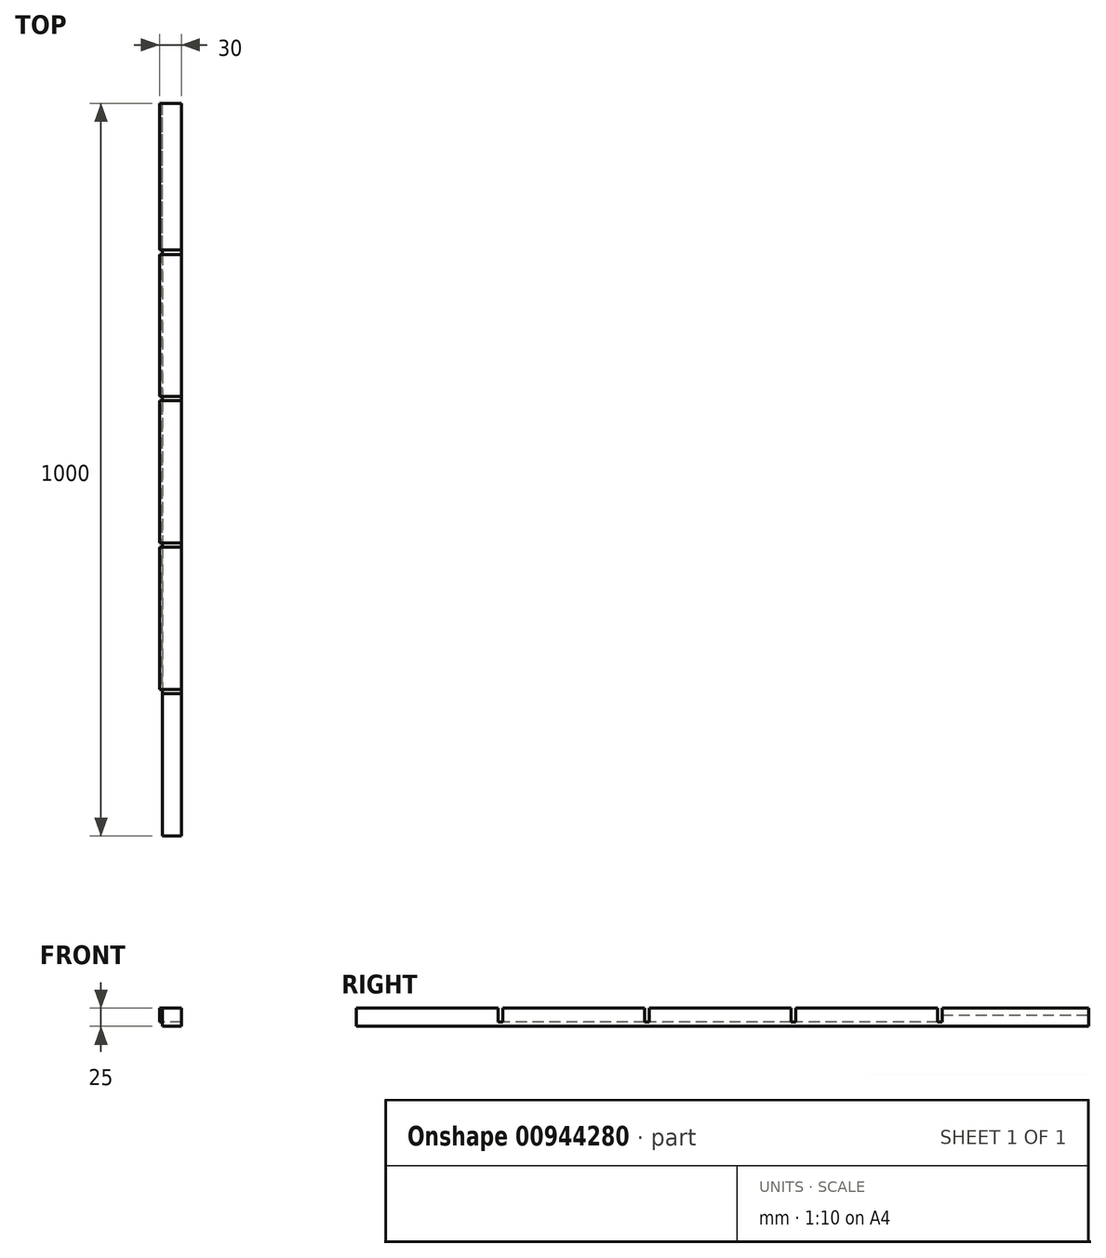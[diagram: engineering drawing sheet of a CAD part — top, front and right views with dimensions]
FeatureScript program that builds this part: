
annotation { "Feature Type Name" : "Feature", "Feature Type Description" : "" }
export const myFeature = defineFeature(function(context is Context, id is Id, definition is map)
    precondition{}
    {
        {
            var Q0;
            Q0=qCreatedBy(makeId("Top.planeOp"),FACE);
            var sketch = newSketch(context, id + "F0", { "sketchPlane" : qUnion([Q0])});
            skLineSegment(sketch, "E0.bottom", {"start": v(0, 0) * mm, "end": v(-30, 0) * mm});
            skLineSegment(sketch, "E0.top", {"start": v(0, 1000) * mm, "end": v(-30, 1000) * mm});
            skLineSegment(sketch, "E0.left", {"start": v(0, 0) * mm, "end": v(0, 1000) * mm});
            skLineSegment(sketch, "E0.right", {"start": v(-30, 0) * mm, "end": v(-30, 1000) * mm});
            skSolve(sketch);
        }
        {
            var Q0;
            Q0 = qSketchRegion(id + "F0", true);
            extrude(context, id + "F1", {"entities" : qUnion([Q0]), "depth" : 25 * mm, "offsetDistance" : 25 * mm});
        }
        {
            var Q0;
            Q0=makeQuery(id+"F1.opExtrude","SWEPT_FACE",FACE,{"disambiguationData":[OSD([sQuery(id+"F0.wireOp",EDGE,"E0.right")])]});
            var sketch = newSketch(context, id + "F2", { "sketchPlane" : qUnion([Q0])});
            skLineSegment(sketch, "E1", {"start": v(-800, 25) * mm, "end": v(-800, 0) * mm, "construction": true});
            skLineSegment(sketch, "E2.bottom", {"start": v(-800, 25) * mm, "end": v(-794, 25) * mm});
            skLineSegment(sketch, "E2.top", {"start": v(-800, 6) * mm, "end": v(-794, 6) * mm});
            skLineSegment(sketch, "E2.left", {"start": v(-800, 25) * mm, "end": v(-800, 6) * mm});
            skLineSegment(sketch, "E2.right", {"start": v(-794, 25) * mm, "end": v(-794, 6) * mm});
            skLineSegment(sketch, "E3.1.0.0", {"start": v(-600, 25) * mm, "end": v(-600, 6) * mm});
            skLineSegment(sketch, "E3.1.0.1", {"start": v(-600, 25) * mm, "end": v(-594, 25) * mm});
            skLineSegment(sketch, "E3.1.0.2", {"start": v(-594, 25) * mm, "end": v(-594, 6) * mm});
            skLineSegment(sketch, "E3.1.0.3", {"start": v(-600, 6) * mm, "end": v(-594, 6) * mm});
            skLineSegment(sketch, "E3.2.0.0", {"start": v(-400, 25) * mm, "end": v(-400, 6) * mm});
            skLineSegment(sketch, "E3.2.0.1", {"start": v(-400, 25) * mm, "end": v(-394, 25) * mm});
            skLineSegment(sketch, "E3.2.0.2", {"start": v(-394, 25) * mm, "end": v(-394, 6) * mm});
            skLineSegment(sketch, "E3.2.0.3", {"start": v(-400, 6) * mm, "end": v(-394, 6) * mm});
            skLineSegment(sketch, "E3.3.0.0", {"start": v(-200, 25) * mm, "end": v(-200, 6) * mm});
            skLineSegment(sketch, "E3.3.0.1", {"start": v(-200, 25) * mm, "end": v(-194, 25) * mm});
            skLineSegment(sketch, "E3.3.0.2", {"start": v(-194, 25) * mm, "end": v(-194, 6) * mm});
            skLineSegment(sketch, "E3.3.0.3", {"start": v(-200, 6) * mm, "end": v(-194, 6) * mm});
            skLineSegment(sketch, "E3.direction1", {"start": v(-800, 6) * mm, "end": v(-600, 6) * mm, "construction": true});
            skSolve(sketch);
        }
        {
            var Q0;
            Q0=makeQuery(id+"F2.imprint","IMPRINT",FACE,{"disambiguationData":[TD([[makeQuery(id+"F2.imprint","IMPRINT",EDGE,{"derivedFrom":sQuery(id+"F2.wireOp",EDGE,"E2.bottom")}),1.0]])]});
            extrude(context, id + "F3", {"entities" : qUnion([Q0]), "operationType" : NewBodyOperationType.REMOVE, "endBound" : BoundingType.THROUGH_ALL, "oppositeDirection" : true, "depth" : 25 * mm, "offsetDistance" : 25 * mm});
        }
        {
            var Q0;
            Q0 = qSketchRegion(id + "F2", true);
            extrude(context, id + "F4", {"entities" : qUnion([Q0]), "operationType" : NewBodyOperationType.REMOVE, "endBound" : BoundingType.THROUGH_ALL, "oppositeDirection" : true, "depth" : 25 * mm, "offsetDistance" : 25 * mm});
        }
        {
            var Q0;
            Q0=makeQuery(id+"F1.opExtrude","SWEPT_FACE",FACE,{"disambiguationData":[OSD([sQuery(id+"F0.wireOp",EDGE,"E0.right")])]});
            var sketch = newSketch(context, id + "F5", { "sketchPlane" : qUnion([Q0])});
            skPoint(sketch, "E4.oppositeSnap0", {"position": v(-194, 15.5) * mm});
            skLineSegment(sketch, "E4.bottom", {"start": v(-194, 6) * mm, "end": v(-1000, 6) * mm});
            skLineSegment(sketch, "E4.top", {"start": v(-194, 15.5) * mm, "end": v(-1000, 15.5) * mm});
            skLineSegment(sketch, "E4.left", {"start": v(-194, 6) * mm, "end": v(-194, 15.5) * mm});
            skLineSegment(sketch, "E4.right", {"start": v(-1000, 6) * mm, "end": v(-1000, 15.5) * mm});
            skSolve(sketch);
        }
        {
            var Q0;
            {var subQ3=sQuery(id+"F5.wireOp",EDGE,"E4.right");Q0=makeQuery(id+"F5.imprint","IMPRINT",FACE,{"disambiguationData":[TD([[makeQuery(id+"F5.imprint","IMPRINT",EDGE,{"derivedFrom":subQ3}),1.0]])]});}
            var Q1;
            {var subQ0=sQuery(id+"F5.wireOp",EDGE,"E4.bottom");var subQ1=makeQuery(id+"F3.boolean.opBoolean","COPY",EDGE,{"derivedFrom":makeQuery(id+"F3.opExtrude","CAP_EDGE",EDGE,{"disambiguationData":[OSD([sQuery(id+"F2.wireOp",EDGE,"E2.right")])],"isStart":true})});var subQ2=makeQuery(id+"F5.imprint","INTERSECT",VERTEX,{"derivedFrom":[subQ1,subQ0]});var subQ3=makeQuery(id+"F4.boolean.opBoolean","COPY",EDGE,{"derivedFrom":makeQuery(id+"F4.opExtrude","CAP_EDGE",EDGE,{"disambiguationData":[OSD([sQuery(id+"F2.wireOp",EDGE,"E3.1.0.0")])],"isStart":true})});var subQ4=makeQuery(id+"F5.imprint","INTERSECT",VERTEX,{"derivedFrom":[subQ3,subQ0]});Q1=makeQuery(id+"F5.imprint","IMPRINT",FACE,{"disambiguationData":[TD([[makeQuery(id+"F5.imprint","IMPRINT",EDGE,{"disambiguationData":[TD([[subQ2,1.0],[subQ4,-1.0]])],"derivedFrom":subQ0}),-1.0]])]});}
            var Q2;
            {var subQ0=sQuery(id+"F5.wireOp",EDGE,"E4.bottom");var subQ1=makeQuery(id+"F4.boolean.opBoolean","COPY",EDGE,{"derivedFrom":makeQuery(id+"F4.opExtrude","CAP_EDGE",EDGE,{"disambiguationData":[OSD([sQuery(id+"F2.wireOp",EDGE,"E3.2.0.2")])],"isStart":true})});var subQ2=makeQuery(id+"F5.imprint","INTERSECT",VERTEX,{"derivedFrom":[subQ1,subQ0]});var subQ3=makeQuery(id+"F4.boolean.opBoolean","COPY",EDGE,{"derivedFrom":makeQuery(id+"F4.opExtrude","CAP_EDGE",EDGE,{"disambiguationData":[OSD([sQuery(id+"F2.wireOp",EDGE,"E3.3.0.0")])],"isStart":true})});var subQ4=makeQuery(id+"F5.imprint","INTERSECT",VERTEX,{"derivedFrom":[subQ3,subQ0]});Q2=makeQuery(id+"F5.imprint","IMPRINT",FACE,{"disambiguationData":[TD([[makeQuery(id+"F5.imprint","IMPRINT",EDGE,{"disambiguationData":[TD([[subQ2,1.0],[subQ4,-1.0]])],"derivedFrom":subQ0}),-1.0]])]});}
            var Q3;
            {var subQ0=sQuery(id+"F5.wireOp",EDGE,"E4.bottom");var subQ1=makeQuery(id+"F4.boolean.opBoolean","COPY",EDGE,{"derivedFrom":makeQuery(id+"F4.opExtrude","CAP_EDGE",EDGE,{"disambiguationData":[OSD([sQuery(id+"F2.wireOp",EDGE,"E3.1.0.2")])],"isStart":true})});var subQ2=makeQuery(id+"F5.imprint","INTERSECT",VERTEX,{"derivedFrom":[subQ1,subQ0]});var subQ3=makeQuery(id+"F4.boolean.opBoolean","COPY",EDGE,{"derivedFrom":makeQuery(id+"F4.opExtrude","CAP_EDGE",EDGE,{"disambiguationData":[OSD([sQuery(id+"F2.wireOp",EDGE,"E3.2.0.0")])],"isStart":true})});var subQ4=makeQuery(id+"F5.imprint","INTERSECT",VERTEX,{"derivedFrom":[subQ3,subQ0]});Q3=makeQuery(id+"F5.imprint","IMPRINT",FACE,{"disambiguationData":[TD([[makeQuery(id+"F5.imprint","IMPRINT",EDGE,{"disambiguationData":[TD([[subQ2,1.0],[subQ4,-1.0]])],"derivedFrom":subQ0}),-1.0]])]});}
            extrude(context, id + "F6", {"entities" : qUnion([Q0, Q1, Q2, Q3]), "operationType" : NewBodyOperationType.REMOVE, "oppositeDirection" : true, "depth" : 4 * mm, "offsetDistance" : 25 * mm});
        }
    });
